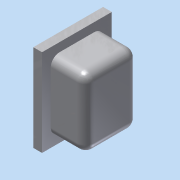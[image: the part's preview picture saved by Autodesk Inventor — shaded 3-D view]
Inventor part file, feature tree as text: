
AUTODESK INVENTOR PART (.ipt)
format: ipt  version: 2015 (Build 190159000, 159)  size: 110,080 bytes
history: native  units: in
note: dims shown in document units (in); Inventor stores cm internally (conversion verified against a paired STEP export)
features: extrude x2, sketch x2, fillet x1, projected_geometry x1
ambient origin geometry x8: Origin, YZ Plane, XZ Plane, XY Plane, X Axis, Y Axis, Z Axis, Center Point
bodies: Solid1 (feature_tree)
feature tree (6):
  extrude  "Extrusion1"  Depth=0.375in
  extrude  "Extrusion2"  Depth=0.0625in
  fillet  "Fillet1"  Radius=0.0625in
  sketch  "Sketch1"  dims[d0=0.5in d1=0.375in]
  sketch  "Sketch2"  dims[d2=0.25in d3=0.0in d4=0.0625in d5=0.0625in d6=0.0in d7=0.0625in]
  projected_geometry  "Projected Loop1"
